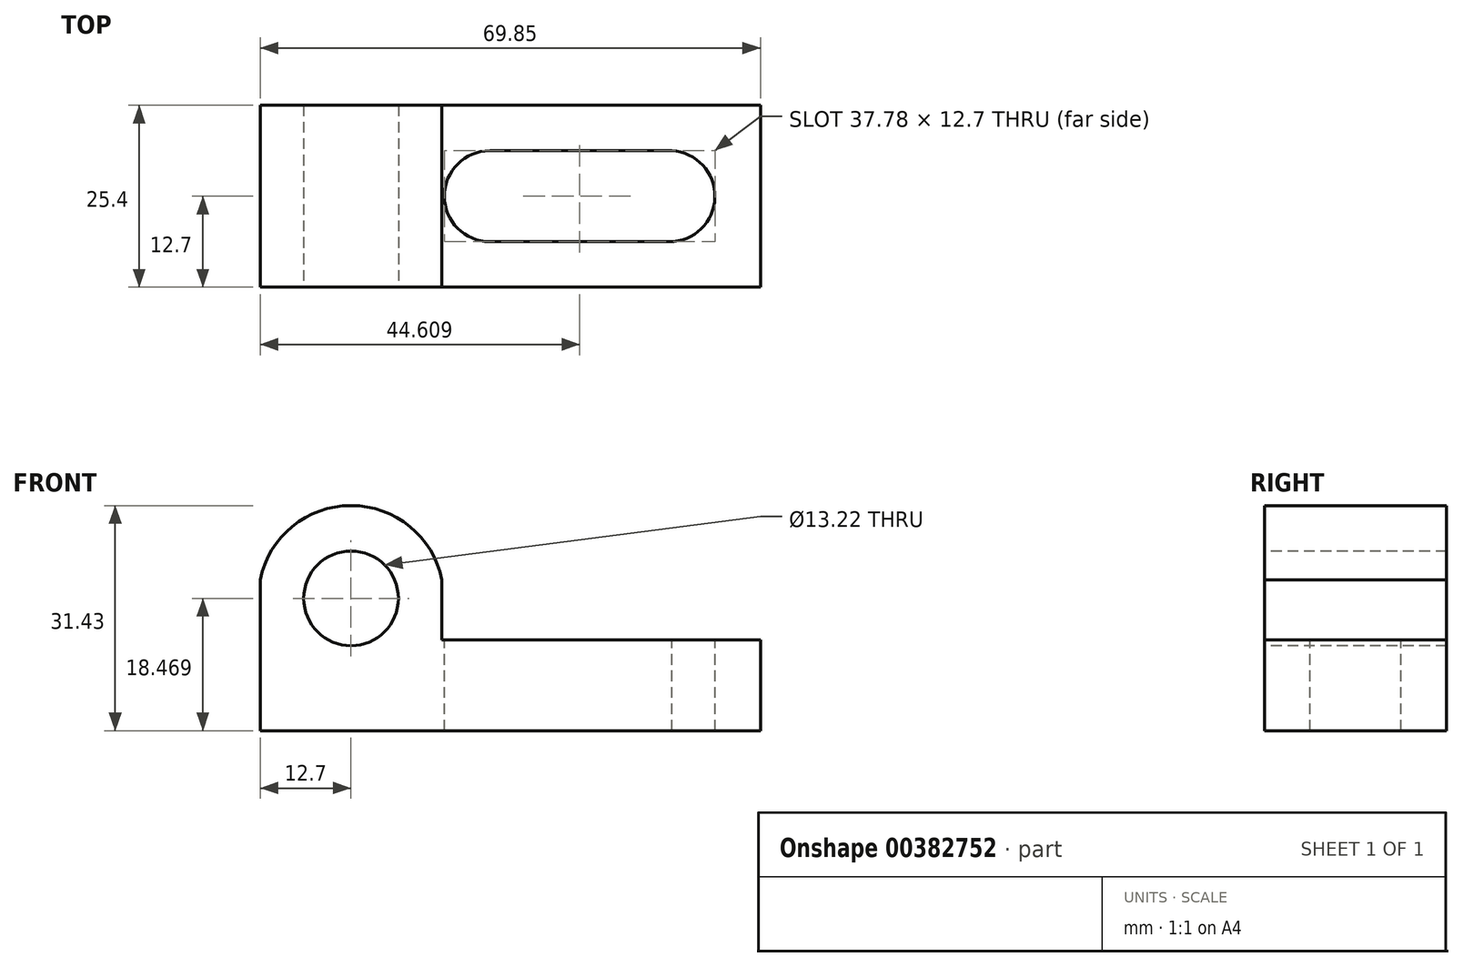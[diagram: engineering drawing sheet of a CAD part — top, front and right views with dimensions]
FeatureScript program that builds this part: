
annotation { "Feature Type Name" : "Feature", "Feature Type Description" : "" }
export const myFeature = defineFeature(function(context is Context, id is Id, definition is map)
    precondition{}
    {
        {
            var Q0;
            Q0=qCreatedBy(makeId("Front.planeOp"),FACE);
            var sketch = newSketch(context, id + "F0", { "sketchPlane" : qUnion([Q0])});
            skLineSegment(sketch, "E0.bottom", {"start": v(0, 0) * mm, "end": v(69.85, 0) * mm});
            skLineSegment(sketch, "E0.top", {"start": v(0, 31.75) * mm, "end": v(69.85, 31.75) * mm});
            skLineSegment(sketch, "E0.left", {"start": v(0, 0) * mm, "end": v(0, 31.75) * mm});
            skLineSegment(sketch, "E0.right", {"start": v(69.85, 0) * mm, "end": v(69.85, 31.75) * mm});
            skSolve(sketch);
        }
        {
            var Q0;
            Q0=makeQuery(id+"F0.imprint","IMPRINT",FACE,{"disambiguationData":[TD([[makeQuery(id+"F0.imprint","IMPRINT",EDGE,{"derivedFrom":sQuery(id+"F0.wireOp",EDGE,"E0.bottom")}),1.0]])]});
            extrude(context, id + "F1", {"entities" : qUnion([Q0]), "depth" : 25.4 * mm});
        }
        {
            var Q0;
            Q0=makeQuery(id+"F1.opExtrude","CAP_FACE",FACE,{"disambiguationData":[OSD([sQuery(id+"F0.wireOp",EDGE,"E0.bottom"),sQuery(id+"F0.wireOp",EDGE,"E0.top"),sQuery(id+"F0.wireOp",EDGE,"E0.left"),sQuery(id+"F0.wireOp",EDGE,"E0.right")])],"isStart":false});
            var sketch = newSketch(context, id + "F2", { "sketchPlane" : qUnion([Q0])});
            skLineSegment(sketch, "E1", {"start": v(25.4, 31.75) * mm, "end": v(25.4, 12.7) * mm});
            skLineSegment(sketch, "E2", {"start": v(25.4, 12.7) * mm, "end": v(69.85, 12.7) * mm});
            skSolve(sketch);
        }
        {
            var Q0;
            Q0 = qSketchRegion(id + "F2", true);
            var Q1;
            {var subQ0=sQuery(id+"F2.wireOp",EDGE,"E1");Q1=makeQuery(id+"F2.imprint","IMPRINT",FACE,{"disambiguationData":[TD([[makeQuery(id+"F2.imprint","IMPRINT",EDGE,{"derivedFrom":subQ0}),1.0]])]});}
            extrude(context, id + "F3", {"entities" : qUnion([Q0, Q1]), "operationType" : NewBodyOperationType.REMOVE, "oppositeDirection" : true, "depth" : 25.4 * mm});
        }
        {
            var Q0;
            Q0=makeQuery(id+"F1.opExtrude","CAP_FACE",FACE,{"disambiguationData":[OSD([sQuery(id+"F0.wireOp",EDGE,"E0.bottom"),sQuery(id+"F0.wireOp",EDGE,"E0.top"),sQuery(id+"F0.wireOp",EDGE,"E0.left"),sQuery(id+"F0.wireOp",EDGE,"E0.right")])],"isStart":false});
            var sketch = newSketch(context, id + "F4", { "sketchPlane" : qUnion([Q0])});
            skArc(sketch, "E3", {"start": v(25.4, 15.88) * mm, "mid": v(12.7, 31.43) * mm, "end": v(0, 15.88) * mm});
            skPoint(sketch, "E3.startSnap0", {"position": v(0, 15.88) * mm});
            skSolve(sketch);
        }
        {
            var Q0;
            Q0 = qSketchRegion(id + "F4", true);
            var Q1;
            {var subQ5=makeQuery(id+"F1.opExtrude","CAP_EDGE",EDGE,{"disambiguationData":[OSD([sQuery(id+"F0.wireOp",EDGE,"E0.top")])],"isStart":false});Q1=makeQuery(id+"F4.imprint","IMPRINT",FACE,{"disambiguationData":[TD([[makeQuery(id+"F4.imprint","IMPRINT",EDGE,{"derivedFrom":subQ5}),-1.0]])]});}
            extrude(context, id + "F5", {"entities" : qUnion([Q0, Q1]), "operationType" : NewBodyOperationType.REMOVE, "oppositeDirection" : true, "depth" : 25.4 * mm});
        }
        {
            var Q0;
            Q0=makeQuery(id+"F1.opExtrude","CAP_FACE",FACE,{"disambiguationData":[OSD([sQuery(id+"F0.wireOp",EDGE,"E0.bottom"),sQuery(id+"F0.wireOp",EDGE,"E0.top"),sQuery(id+"F0.wireOp",EDGE,"E0.left"),sQuery(id+"F0.wireOp",EDGE,"E0.right")])],"isStart":false});
            var sketch = newSketch(context, id + "F6", { "sketchPlane" : qUnion([Q0])});
            skCircle(sketch, "E4", {"center": v(12.7, 18.47) * mm, "radius": 6.61 * mm});
            skSolve(sketch);
        }
        {
            var Q0;
            Q0=makeQuery(id+"F6.imprint","IMPRINT",FACE,{"disambiguationData":[TD([[makeQuery(id+"F6.imprint","IMPRINT",EDGE,{"derivedFrom":sQuery(id+"F6.wireOp",EDGE,"E4")}),1.0]])]});
            extrude(context, id + "F7", {"entities" : qUnion([Q0]), "operationType" : NewBodyOperationType.REMOVE, "oppositeDirection" : true, "depth" : 25.4 * mm});
        }
        {
            var Q0;
            Q0=makeQuery(id+"F3.boolean.opBoolean","COPY",FACE,{"derivedFrom":makeQuery(id+"F3.opExtrude","SWEPT_FACE",FACE,{"disambiguationData":[OSD([sQuery(id+"F2.wireOp",EDGE,"E2")])]})});
            var sketch = newSketch(context, id + "F8", { "sketchPlane" : qUnion([Q0])});
            skLineSegment(sketch, "E5", {"start": v(32.07, -6.35) * mm, "end": v(57.47, -6.35) * mm});
            skLineSegment(sketch, "E6", {"start": v(31.75, -19.05) * mm, "end": v(57.15, -19.05) * mm});
            skArc(sketch, "E7", {"start": v(57.15, -19.05) * mm, "mid": v(63.5, -12.86) * mm, "end": v(57.47, -6.35) * mm});
            skArc(sketch, "E8", {"start": v(32.07, -6.35) * mm, "mid": v(25.72, -12.7) * mm, "end": v(32.07, -19.05) * mm});
            skSolve(sketch);
        }
        {
            var Q0;
            Q0=makeQuery(id+"F8.imprint","IMPRINT",FACE,{"disambiguationData":[TD([[makeQuery(id+"F8.imprint","IMPRINT",EDGE,{"derivedFrom":sQuery(id+"F8.wireOp",EDGE,"E5")}),-1.0]])]});
            extrude(context, id + "F9", {"entities" : qUnion([Q0]), "operationType" : NewBodyOperationType.REMOVE, "oppositeDirection" : true, "depth" : 25.4 * mm});
        }
        {
            var Q0;
            Q0=makeQuery(id+"F3.boolean.opBoolean","COPY",FACE,{"derivedFrom":makeQuery(id+"F3.opExtrude","SWEPT_FACE",FACE,{"disambiguationData":[OSD([sQuery(id+"F2.wireOp",EDGE,"E2")])]})});
            var sketch = newSketch(context, id + "F10", { "sketchPlane" : qUnion([Q0])});
            skArc(sketch, "E9", {"start": v(62.52, -25.4) * mm, "mid": v(69.74, -11.63) * mm, "end": v(59.43, 0) * mm});
            skSolve(sketch);
        }
        {
            var Q0;
            {var subQ0=sQuery(id+"F10.wireOp",EDGE,"E9");Q0=makeQuery(id+"F10.imprint","IMPRINT",FACE,{"disambiguationData":[TD([[makeQuery(id+"F10.imprint","IMPRINT",EDGE,{"derivedFrom":subQ0}),-1.0]])]});}
            extrude(context, id + "F11", {"entities" : qUnion([Q0]), "operationType" : NewBodyOperationType.REMOVE, "depth" : 25.4 * mm});
        }
    });
